# Revit family: M_灑水頭 - 懸吊式 - 半嵌壁式 - 主體
name_source: partatom
category: Sprinklers
revit_build: Autodesk Revit 2017 (Build: 20160109_1515(x64)
units: mm (PartAtom-declared; Revit-internal decimal feet)

## family parameters
Cut with Voids When Loaded = No
Host = Face
Maintain Annotation Orientation = Yes
OmniClass Number = 23.65.70.17.11.24
OmniClass Title = Fire Fighting Sprinkler Heads
Part Type = Normal
Room Calculation Point = No
Round Connector Dimension = Use Radius
Shared = No

## types (8) — shared parameters
Coverage = Standard
Default Elevation = 2400 mm
Orifice = Standard
Pressure Class = Standard
Response = Standard
Temperature Rating = 57 °C
孔罩半徑 = 38 mm
孔罩厚度 = 3 mm
孔罩直徑 = 75 mm

## per-type parameters (varying)
| type | CEL | K-Factor | Orifice Size | 整體長度 | 標稱直徑 | 標稱直徑半徑 | 突出 |
| 15 mm 滴狀 | 7 mm | 81 | 13 mm | 60 mm | 15 mm | 8 mm | 30 mm |
| 15 mm 滴狀下垂 | 7 mm | 81 | 13 mm | 60 mm | 15 mm | 8 mm | 30 mm |
| 15 mm 滴狀下垂帶托架 | 7 mm | 81 | 13 mm | 60 mm | 15 mm | 8 mm | 30 mm |
| 15 mm 滴狀帶托架 | 7 mm | 81 | 13 mm | 60 mm | 15 mm | 8 mm | 30 mm |
| 20 mm 滴狀 | 10 mm | 115 | 14 mm | 64 mm | 20 mm | 10 mm | 34 mm |
| 20 mm 滴狀下垂 | 10 mm | 115 | 14 mm | 64 mm | 20 mm | 10 mm | 34 mm |
| 20 mm 滴狀下垂帶托架 | 10 mm | 115 | 14 mm | 64 mm | 20 mm | 10 mm | 34 mm |
| 20 mm 滴狀帶托架 | 10 mm | 115 | 14 mm | 64 mm | 20 mm | 10 mm | 34 mm |

## geometry (parser evidence)
native form markers: Sweep x1
no freeform markers — native parametric forms only
